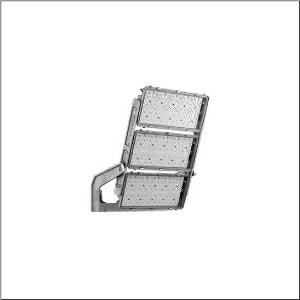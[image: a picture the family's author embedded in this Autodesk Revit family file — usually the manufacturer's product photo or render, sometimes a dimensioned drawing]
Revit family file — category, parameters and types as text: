
# Revit family: floodlight_fl_11_maxi_pro_remote___pl43_5xa779426a01ba_bd65
name_source: partatom
category: Lighting Fixtures
units: mm (PartAtom-declared; Revit-internal decimal feet)

## family parameters
Cut with Voids When Loaded = No
Host = Face
Light Source = No
Part Type = Normal
Room Calculation Point = No
Round Connector Dimension = Use Diameter
Shared = No

## types (1)
- --- (1 x LED, 149370 lm, 1095.8 W, 4000K)
    Apparent Load = 1096 VA
    CIE Flux Codes = 25 74 99 100 100
    Color Rendering = 70
    Color Temperature = 4000K
    Default Elevation = 1800 mm
    Description = Floodlight FL 11  maxi  pro Remote floodlight; light control with lens of PMMA; cover panel of toughened safety glass, transparent; light distribution: PL43, asymmetric direct distribution, LEDcolour temperature: 4000K, colour rendering: CRI > 70, light colour: 740; brightness control: DALI 2 (1 DALI address); with terminal, 8-pole, max. 2.5mm², mains connection: 220..240V/380..400V AC, 50/60Hz, surge voltage resistance: line to ground: 10kV, ECG replaceable separately, no afterglow with DALI off / DMX off command, LED unit replaceable without ESD environment, dustproof LED module, dimming range 10..100%; floodlight with 2x LED unit of diecast aluminium, coated grey; length: 713mm / width: 651mm / height: 338mm; mounting bracket, of diecast aluminium, uncoated, natural, equipment: Power, protection rating (complete): IP66; insulation class (complete): insulation class I (protective earthing); certification: CE, ENEC, VDE; ball protection: ball impact resistance with accessories, only for outdoor installations, rated ambient temperature 10°C, permissible operating ambient temperature: -40..+30°C, permissible storage temperature: -40..+85°C; packaging unit: 1 piece

Light Distribution: PL43
    Height = 320 mm
    Lamp = 1 x LED
    Lamp Light Flux = 149370 lm
    Lamp Power = 1095.8 W
    Lamp count = 1
    Length = 1002 mm
    Luminous efficacy = 136 lm/W
    Manufacturer = Siteco
    ModVariant = No
    Model = 5XA779426A01BA
    Number of Poles = 1
    OnlyDefault = Yes
    Power Factor = 1
    Product Name = Floodlight FL 11 maxi pro Remote | PL43
    Product group = floodlight | pylon top
    ProductGroupID = 6101
    Protection Class = Protection class I
    Protection Degree = IP 66
    RLX_Detail_Level = 1
    RlxData = <blob elided: 52429 chars, md5=9c754e3a>
    Socket = socket
    Standby Power = 0 W
    System Light Flux = 149370 lm
    System Power = 1096 W
    Type Comments = factory setting: luminous flux: 100 % | dim-lin: 254 | 760 mA
    Type Image = l_1006784.jpg
    URL = http://relux.com
    VarID = @adj_005951
    Voltage = 0 V
    Weight = 0.00 kg
    Width = 655 mm

## geometry (parser evidence)
native form markers: Blend x4, Sweep x15
no freeform markers — native parametric forms only
